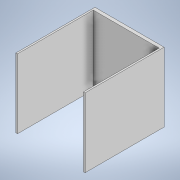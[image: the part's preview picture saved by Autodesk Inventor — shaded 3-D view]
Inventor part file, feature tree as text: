
AUTODESK INVENTOR PART (.ipt)
format: ipt  version: 2021.1 (Build 251245010, 245A)  size: 98,816 bytes
history: native  units: mm
features: extrude x2, sketch x2
ambient origin geometry x8: Origin, YZ Plane, XZ Plane, XY Plane, X Axis, Y Axis, Z Axis, Center Point
bodies: Solid1 (feature_tree)
feature tree (4):
  extrude  "Extrusion1"  Depth=120.0mm TaperAngle=0.0deg
  extrude  "Extrusion2"  Depth=115.0mm
  sketch  "Sketch2"  dims[d1=105.0mm d2=120.0mm d3=0.0mm]
  sketch  "Sketch3"  dims[d4=100.0mm d5=114.0mm d6=115.0mm d7=0.0mm]
